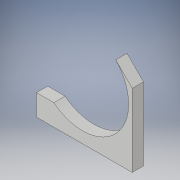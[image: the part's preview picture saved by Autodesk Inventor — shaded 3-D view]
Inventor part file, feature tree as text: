
AUTODESK INVENTOR PART (.ipt)
format: ipt  version: 2018 (Build 220112000, 112)  size: 105,984 bytes
history: native  units: in
note: dims shown in document units (in); Inventor stores cm internally (conversion verified against a paired STEP export)
features: extrude x1, sketch x1
ambient origin geometry x8: Origin, YZ Plane, XZ Plane, XY Plane, X Axis, Y Axis, Z Axis, Center Point
bodies: Solid1 (feature_tree)
feature tree (2):
  extrude  "Extrusion1"  TaperAngle=135.0deg  [1 undecoded]
  sketch  "Sketch1"  dims[d0=16.375in d3=135.0deg d4=2.0in d5=0.0in d6=17.0in]
note: 1 required parameter value undecoded (feature->parameter linkage not recoverable at this tier; creation-order binding heuristic only, values carry confidence <= 0.55)
